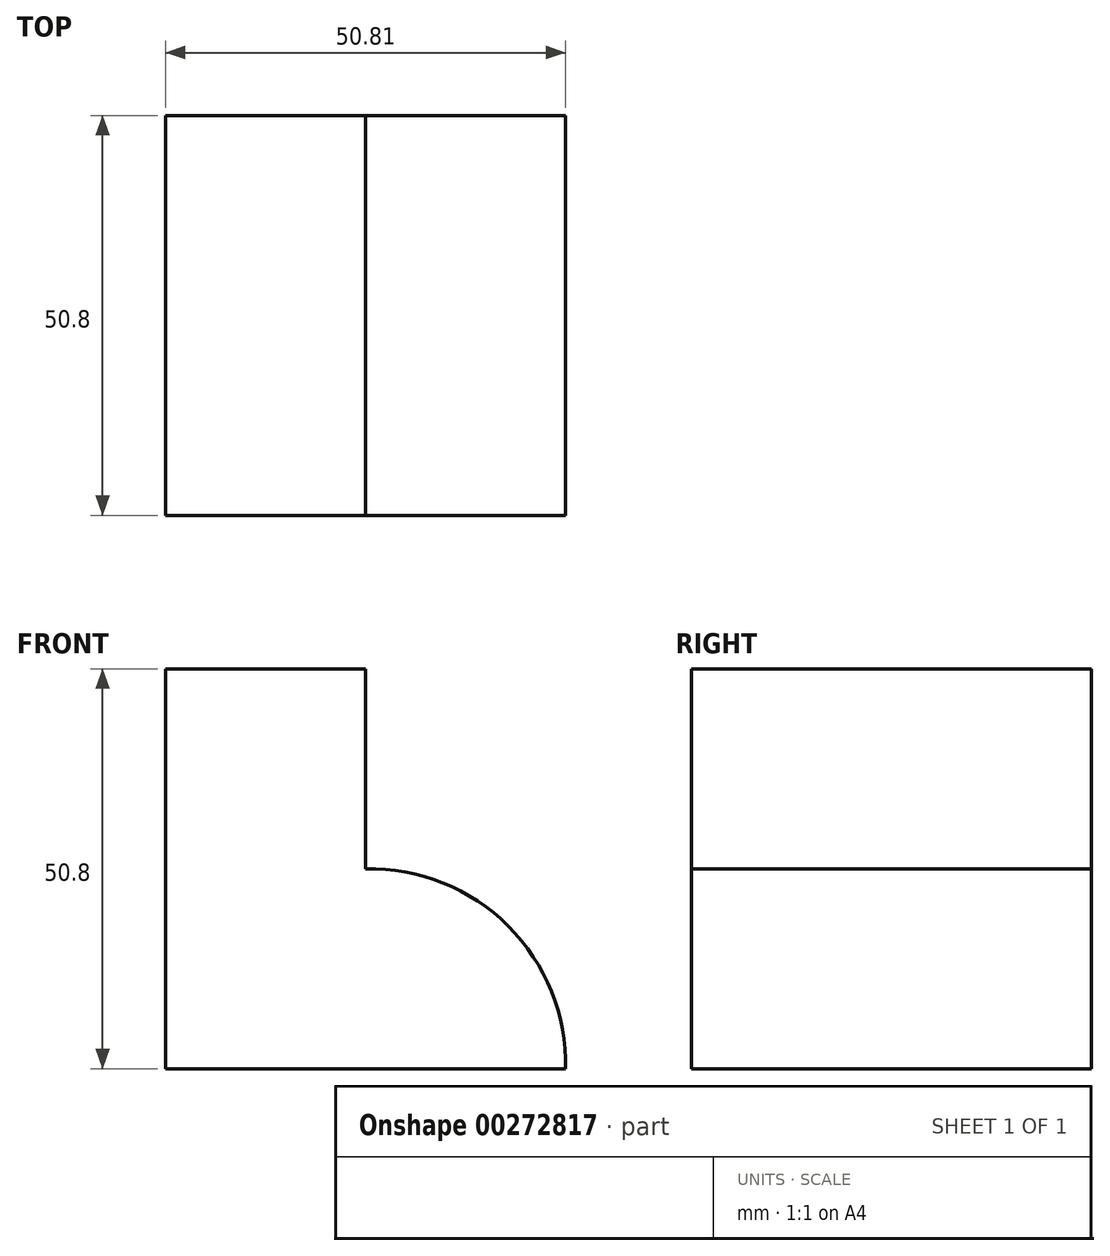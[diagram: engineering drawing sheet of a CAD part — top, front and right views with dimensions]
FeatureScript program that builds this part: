
annotation { "Feature Type Name" : "Feature", "Feature Type Description" : "" }
export const myFeature = defineFeature(function(context is Context, id is Id, definition is map)
    precondition{}
    {
        {
            var Q0;
            Q0=qCreatedBy(makeId("Front.planeOp"),FACE);
            var sketch = newSketch(context, id + "F0", { "sketchPlane" : qUnion([Q0])});
            skLineSegment(sketch, "E0", {"start": v(0, 0) * mm, "end": v(-50.8, 0) * mm});
            skLineSegment(sketch, "E1", {"start": v(-50.8, 0) * mm, "end": v(-50.8, 50.8) * mm});
            skLineSegment(sketch, "E2", {"start": v(-50.8, 50.8) * mm, "end": v(-25.4, 50.8) * mm});
            skLineSegment(sketch, "E3", {"start": v(-25.4, 50.8) * mm, "end": v(-25.4, 25.4) * mm});
            skArc(sketch, "E4", {"start": v(0, 0) * mm, "mid": v(-7.27, 18.13) * mm, "end": v(-25.4, 25.4) * mm});
            skSolve(sketch);
        }
        {
            var Q0;
            Q0=makeQuery(id+"F0.imprint","IMPRINT",FACE,{"disambiguationData":[TD([[makeQuery(id+"F0.imprint","IMPRINT",EDGE,{"derivedFrom":sQuery(id+"F0.wireOp",EDGE,"E0")}),-1.0]])]});
            extrude(context, id + "F1", {"entities" : qUnion([Q0]), "depth" : 50.8 * mm});
        }
    });
